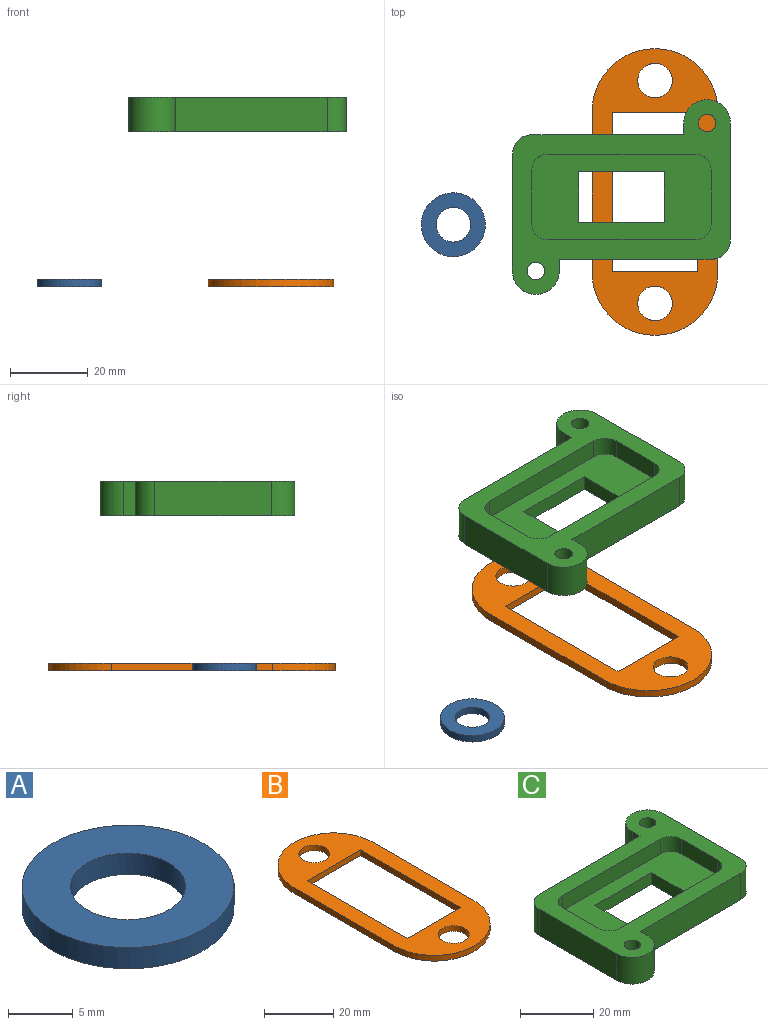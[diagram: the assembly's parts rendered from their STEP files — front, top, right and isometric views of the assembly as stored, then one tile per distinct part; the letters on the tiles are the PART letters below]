
ASSEMBLY  parts=3 mates=2
PART A: 4 faces, bbox 16.4x16.4x2 mm
  f0: cylinder r=8.2mm len=16.4mm, axis (0,0,-1), area 103mm2, adj f1,f2
  f1: plane 16.4x16.4mm, normal (0,0,1), area 149mm2, adj f0,f3
  f2: plane 16.4x16.4mm, normal (0,0,-1), area 149mm2, adj f0,f3
  f3: cylinder r=4.45mm len=8.9mm, axis (0,0,-1), area 55.9mm2, adj f1,f2
PART B: 12 faces, bbox 32.3x73.6x2 mm
  f0: plane 41.3x2mm, normal (1,0,0), area 82.6mm2, adj f1,f7,f8,f9
  f1: cylinder r=16.15mm len=32.3mm, axis (0,0,-1), area 101.5mm2, adj f0,f2,f8,f9
  f2: plane 41.3x2mm, normal (-1,0,0), area 82.6mm2, adj f1,f7,f8,f9
  f3: plane 41x2mm, normal (1,0,0), area 82mm2, adj f4,f6,f8,f9
  f4: plane 22x2mm, normal (0,-1,0), area 44mm2, adj f3,f5,f8,f9
  f5: plane 41x2mm, normal (-1,0,0), area 82mm2, adj f4,f6,f8,f9
  f6: plane 22x2mm, normal (0,1,0), area 44mm2, adj f3,f5,f8,f9
  f7: cylinder r=16.15mm len=32.3mm, axis (0,0,-1), area 101.5mm2, adj f0,f2,f8,f9
  f8: plane 73.6x32.3mm, normal (0,0,1), area 1127mm2, adj f0,f1,f2,f3,f4,f5,f6,f7
  f9: plane 73.6x32.3mm, normal (0,0,-1), area 1127mm2, adj f0,f1,f2,f3,f4,f5,f6,f7
  f10: cylinder r=4.45mm len=8.9mm, axis (0,0,-1), area 55.9mm2, adj f8,f9
  f11: cylinder r=4.45mm len=8.9mm, axis (0,0,-1), area 55.9mm2, adj f8,f9
PART C: 27 faces, bbox 56x50x8.9 mm
  f0: plane 13x3.9mm, normal (1,0,0), area 50.7mm2, adj f1,f3,f15,f26
  f1: plane 22x3.9mm, normal (0,-1,0), area 85.8mm2, adj f0,f2,f15,f26
  f2: plane 13x3.9mm, normal (-1,0,0), area 50.7mm2, adj f1,f3,f15,f26
  f3: plane 22x3.9mm, normal (0,1,0), area 85.8mm2, adj f0,f2,f15,f26
  f4: plane 39x8.9mm, normal (0,1,0), area 347.1mm2, adj f5,f13,f14,f15
  f5: cylinder r=5mm len=8.9mm, axis (0,0,-1), area 69.9mm2, adj f4,f6,f14,f15
  f6: plane 30x8.9mm, normal (-1,0,0), area 267mm2, adj f5,f7,f14,f15
  f7: cylinder r=6mm len=12mm, axis (0,0,-1), area 167.8mm2, adj f6,f8,f14,f15
  f8: plane 8.9x3mm, normal (1,0,0), area 26.7mm2, adj f7,f9,f14,f15
  f9: plane 39x8.9mm, normal (0,-1,0), area 347.1mm2, adj f8,f10,f14,f15
  f10: cylinder r=5mm len=8.9mm, axis (0,0,-1), area 69.9mm2, adj f9,f11,f14,f15
  f11: plane 30x8.9mm, normal (1,0,0), area 267mm2, adj f10,f12,f14,f15
  f12: cylinder r=6mm len=12mm, axis (0,0,-1), area 167.8mm2, adj f11,f13,f14,f15
  f13: plane 8.9x3mm, normal (-1,0,0), area 26.7mm2, adj f4,f12,f14,f15
  f14: plane 56x50mm, normal (0,0,1), area 936.3mm2, adj f4,f5,f6,f7,f8,f9,f10,f11
  f15: plane 56x50mm, normal (0,0,-1), area 1648.6mm2, adj f0,f1,f2,f3,f4,f5,f6,f7
  f16: cylinder r=2.25mm len=8.9mm, axis (0,0,-1), area 125.8mm2, adj f14,f15
  f17: cylinder r=2.25mm len=8.9mm, axis (0,0,-1), area 125.8mm2, adj f14,f15
  f18: plane 14x5mm, normal (1,0,0), area 70mm2, adj f14,f19,f25,f26
  f19: cylinder r=4mm len=5mm, axis (0,0,1), area 31.4mm2, adj f14,f18,f20,f26
  f20: plane 38x5mm, normal (0,1,0), area 190mm2, adj f14,f19,f21,f26
  f21: cylinder r=4mm len=5mm, axis (0,0,1), area 31.4mm2, adj f14,f20,f22,f26
  f22: plane 14x5mm, normal (-1,0,0), area 70mm2, adj f14,f21,f23,f26
  f23: cylinder r=4mm len=5mm, axis (0,0,1), area 31.4mm2, adj f14,f22,f24,f26
  f24: plane 38x5mm, normal (0,-1,0), area 190mm2, adj f14,f23,f25,f26
  f25: cylinder r=4mm len=5mm, axis (0,0,1), area 31.4mm2, adj f14,f18,f24,f26
  f26: plane 46x22mm, normal (0,0,1), area 712.3mm2, adj f0,f1,f2,f3,f18,f19,f20,f21
PLACE A t=(-9.31,0.33,16.31)mm
PLACE B t=(7.74,8.75,16.31)mm
PLACE C t=(-0.87,7.37,56.2)mm
MATE parallel B.f8 <-> C.f15  axis (0,0,1) through (7.74,8.75,18.31)mm
MATE parallel A.f0 <-> B.f8  axis (0,0,1) through (-44.06,0.33,18.31)mm
